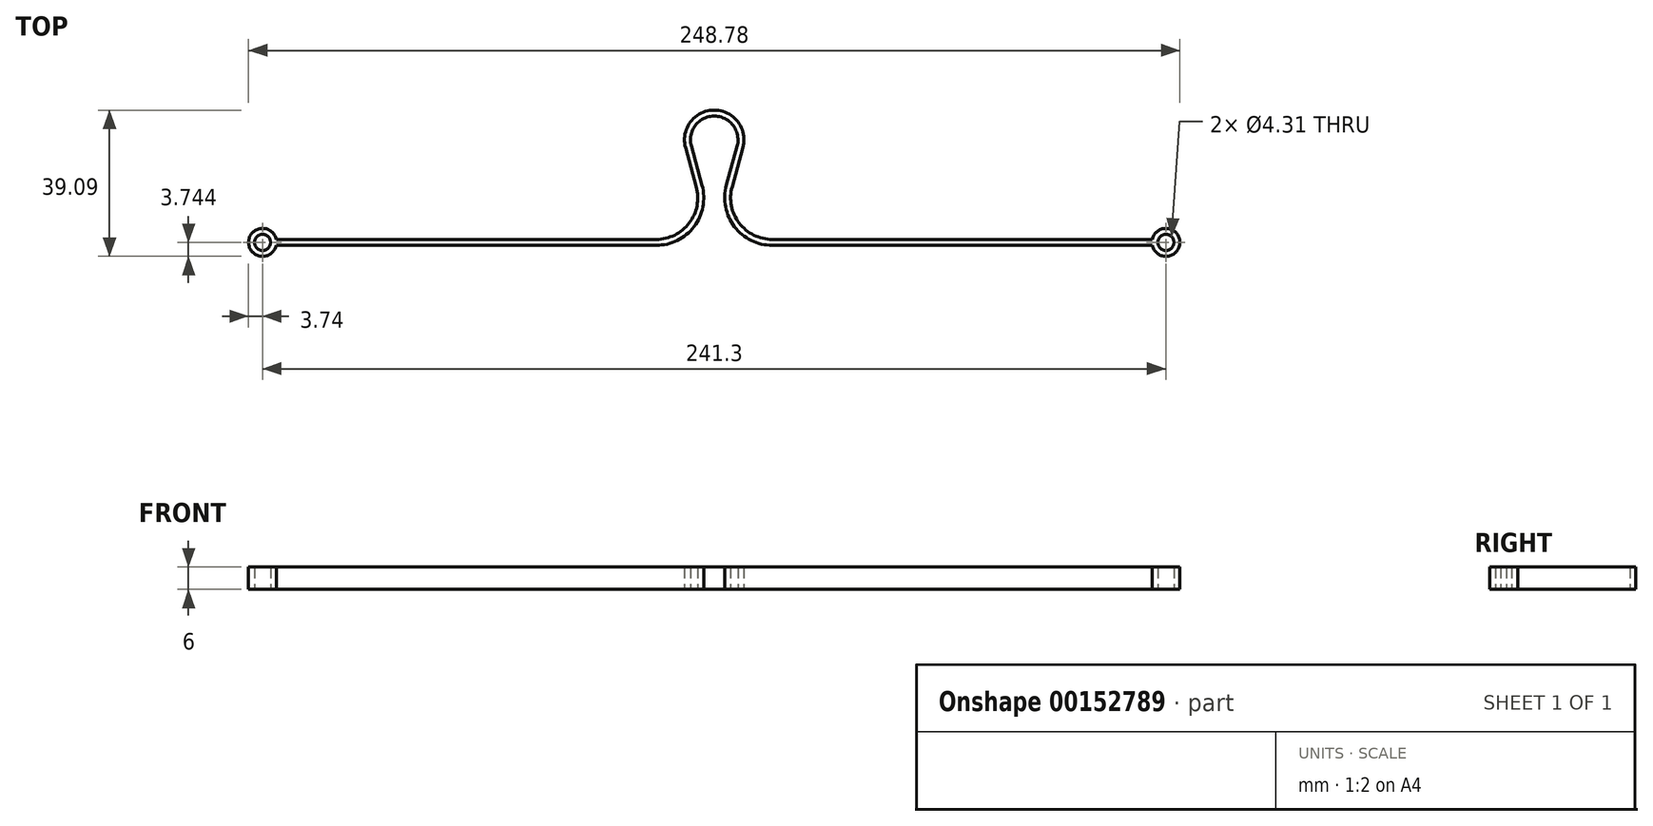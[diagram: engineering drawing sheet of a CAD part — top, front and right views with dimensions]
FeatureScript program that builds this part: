
annotation { "Feature Type Name" : "Feature", "Feature Type Description" : "" }
export const myFeature = defineFeature(function(context is Context, id is Id, definition is map)
    precondition{}
    {
        {
            var Q0;
            Q0=qCreatedBy(makeId("Top.planeOp"),FACE);
            var sketch = newSketch(context, id + "F0", { "sketchPlane" : qUnion([Q0])});
            skLineSegment(sketch, "E0", {"start": v(0, 0) * mm, "end": v(0, -15.5) * mm, "construction": true});
            skLineSegment(sketch, "E1", {"start": v(-15.5, -15.5) * mm, "end": v(15.5, -15.5) * mm, "construction": true});
            skArc(sketch, "E2", {"start": v(6.12, -1.68) * mm, "mid": v(0, 6.35) * mm, "end": v(-6.12, -1.68) * mm});
            skArc(sketch, "E3", {"start": v(-15.5, -26.61) * mm, "mid": v(-6.66, -22.24) * mm, "end": v(-4.78, -12.56) * mm});
            skArc(sketch, "E4", {"start": v(-15.5, -28.2) * mm, "mid": v(-5.4, -23.2) * mm, "end": v(-3.25, -12.14) * mm});
            skArc(sketch, "E5", {"start": v(7.65, -2.1) * mm, "mid": v(0, 7.94) * mm, "end": v(-7.65, -2.1) * mm});
            skLineSegment(sketch, "E6", {"start": v(-6.12, -1.68) * mm, "end": v(-3.25, -12.14) * mm});
            skLineSegment(sketch, "E7", {"start": v(-7.65, -2.1) * mm, "end": v(-4.78, -12.56) * mm});
            skLineSegment(sketch, "E8", {"start": v(-15.5, -26.61) * mm, "end": v(-117, -26.61) * mm});
            skLineSegment(sketch, "E9", {"start": v(-15.5, -28.2) * mm, "end": v(-117, -28.2) * mm});
            skArc(sketch, "E10", {"start": v(-117, -26.61) * mm, "mid": v(-124.4, -27.4) * mm, "end": v(-117, -28.2) * mm});
            skLineSegment(sketch, "E11", {"start": v(-117, -26.61) * mm, "end": v(-117, -28.2) * mm, "construction": true});
            skCircle(sketch, "E12", {"center": v(-120.65, -27.4) * mm, "radius": 2.15 * mm});
            skLineSegment(sketch, "E13", {"start": v(6.12, -1.68) * mm, "end": v(3.25, -12.14) * mm});
            skLineSegment(sketch, "E14", {"start": v(7.65, -2.1) * mm, "end": v(4.78, -12.56) * mm});
            skArc(sketch, "E15", {"start": v(3.25, -12.14) * mm, "mid": v(5.4, -23.2) * mm, "end": v(15.5, -28.2) * mm});
            skArc(sketch, "E16", {"start": v(4.78, -12.56) * mm, "mid": v(6.66, -22.24) * mm, "end": v(15.5, -26.61) * mm});
            skLineSegment(sketch, "E17", {"start": v(15.5, -26.61) * mm, "end": v(117, -26.61) * mm});
            skLineSegment(sketch, "E18", {"start": v(15.5, -28.2) * mm, "end": v(117, -28.2) * mm});
            skArc(sketch, "E19", {"start": v(117, -28.2) * mm, "mid": v(124.4, -27.4) * mm, "end": v(117, -26.61) * mm});
            skLineSegment(sketch, "E20", {"start": v(117, -28.2) * mm, "end": v(117, -26.61) * mm, "construction": true});
            skCircle(sketch, "E21", {"center": v(120.65, -27.4) * mm, "radius": 2.15 * mm});
            skSolve(sketch);
        }
        {
            var Q0;
            Q0 = qSketchRegion(id + "F0", true);
            extrude(context, id + "F1", {"entities" : qUnion([Q0]), "depth" : 6 * mm});
        }
    });
